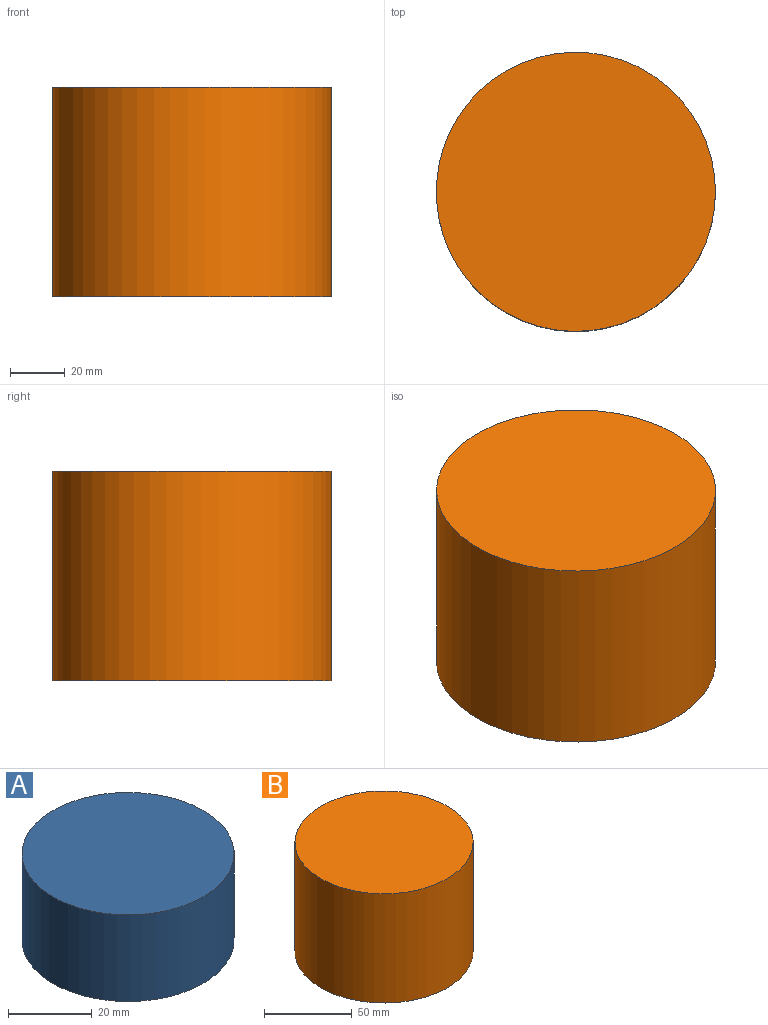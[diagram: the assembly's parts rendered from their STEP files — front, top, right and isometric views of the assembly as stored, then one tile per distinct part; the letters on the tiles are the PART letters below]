
ASSEMBLY  parts=2 mates=1
PART A: 5 faces, bbox 50.8x50.8x25.4 mm
  f0: cylinder r=25.4mm len=50.8mm, axis (0,0,-1), area 4053.7mm2, adj f1,f2
  f1: plane 50.8x50.8mm, normal (0,0,1), area 2026.8mm2, adj f0
  f2: plane 50.8x50.8mm, normal (0,0,-1), area 475mm2, adj f0,f3
  f3: cylinder r=22.23mm len=44.45mm, axis (0,0,-1), area 2660.2mm2, adj f2,f4
  f4: plane 44.45x44.45mm, normal (0,0,-1), area 1551.8mm2, adj f3
PART B: 5 faces, bbox 101.6x101.6x76.2 mm
  f0: cylinder r=50.8mm len=101.6mm, axis (0,0,-1), area 24322mm2, adj f1,f2
  f1: plane 101.6x101.6mm, normal (0,0,1), area 8107.3mm2, adj f0
  f2: plane 101.6x101.6mm, normal (0,0,-1), area 981.7mm2, adj f0,f3
  f3: cylinder r=47.62mm len=95.25mm, axis (0,0,-1), area 20901.7mm2, adj f2,f4
  f4: plane 95.25x95.25mm, normal (0,0,-1), area 7125.6mm2, adj f3
PLACE A t=(27.06,28.71,25.98)mm
PLACE B t=(27.06,28.71,-18.47)mm
MATE slider A.f0 <-> B.f0  axis (0,0,1) through (27.06,28.71,51.38)mm
